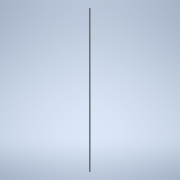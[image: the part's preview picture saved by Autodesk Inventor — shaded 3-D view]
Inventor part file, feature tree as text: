
AUTODESK INVENTOR PART (.ipt)
format: ipt  version: 2022 (Build 260153000, 153)  size: 149,504 bytes
history: native  units: mm
features: extrude x1, sketch x1
ambient origin geometry x8: Origin, YZ Plane, XZ Plane, XY Plane, X Axis, Y Axis, Z Axis, Center Point
bodies: Body1 (feature_tree)
feature tree (2):
  extrude  "Extrusion7"  Depth=5.0mm
  sketch  "Sketch4"  dims[d31=34.456mm d103=5.0mm d104=5.0mm d105=1456.0mm d106=0.0mm]
